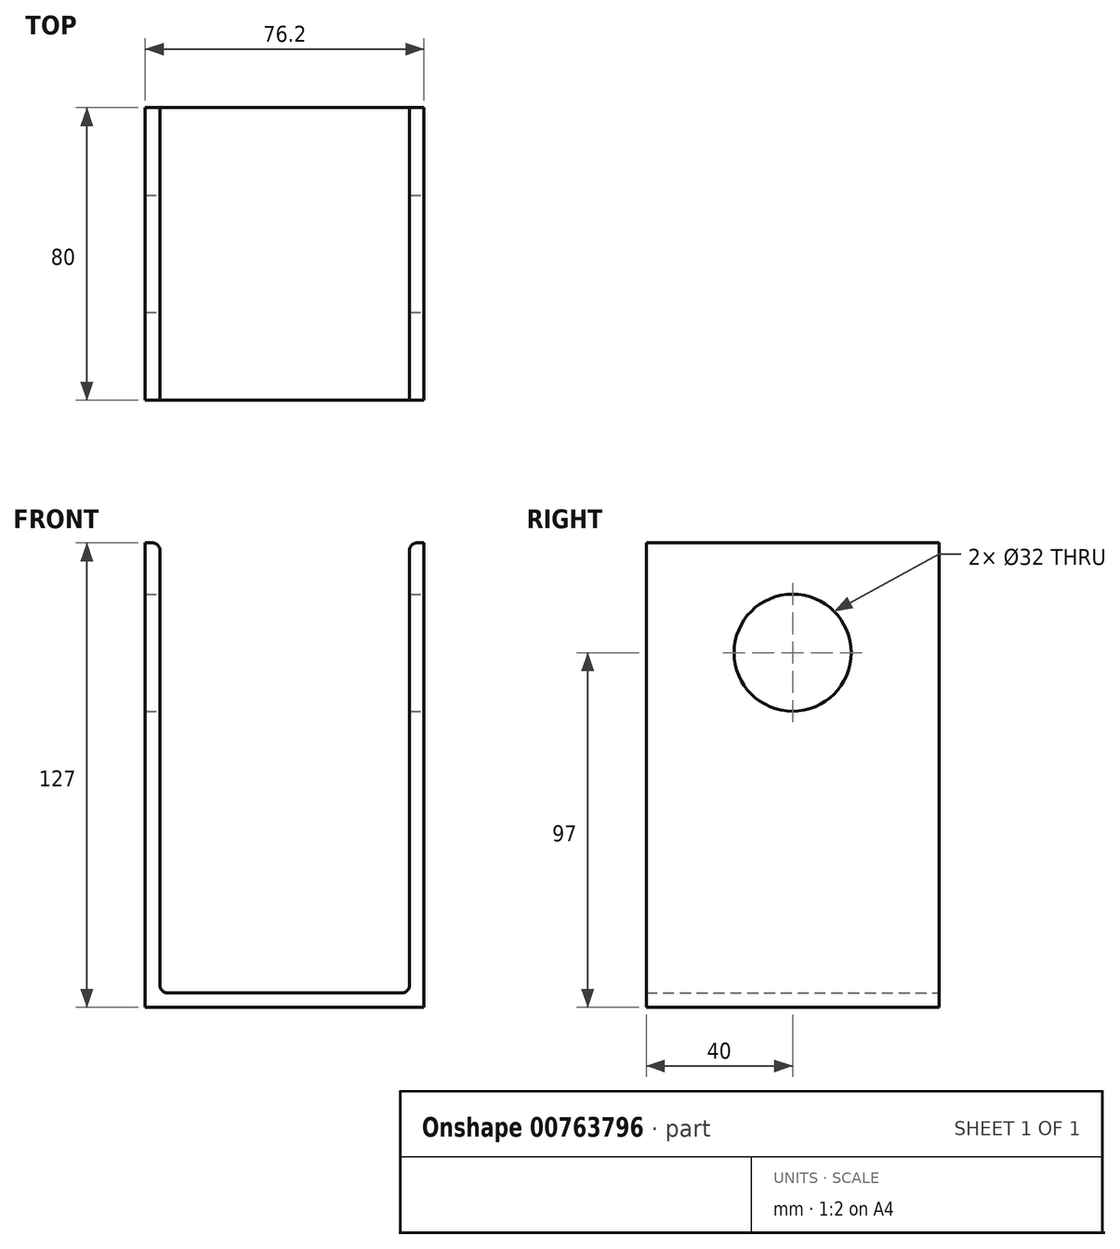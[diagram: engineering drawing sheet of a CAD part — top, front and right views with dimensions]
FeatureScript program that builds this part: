
annotation { "Feature Type Name" : "Feature", "Feature Type Description" : "" }
export const myFeature = defineFeature(function(context is Context, id is Id, definition is map)
    precondition{}
    {
        {
            var Q0;
            Q0=qCreatedBy(makeId("Front.planeOp"),FACE);
            var sketch = newSketch(context, id + "F0", { "sketchPlane" : qUnion([Q0])});
            skLineSegment(sketch, "E0", {"start": v(-38.1, 0) * mm, "end": v(0, 0) * mm});
            skLineSegment(sketch, "E1", {"start": v(-38.1, 0) * mm, "end": v(-38.1, 127) * mm});
            skLineSegment(sketch, "E2.0", {"start": v(-34.1, 6) * mm, "end": v(-34.1, 125) * mm});
            skLineSegment(sketch, "E2.1", {"start": v(-32.1, 4) * mm, "end": v(0, 4) * mm});
            skLineSegment(sketch, "E3", {"start": v(-38.1, 127) * mm, "end": v(-36.1, 127) * mm});
            skPoint(sketch, "E4.visualSharp", {"position": v(-34.1, 127) * mm});
            skArc(sketch, "E4.filletArc", {"start": v(-34.1, 125) * mm, "mid": v(-34.69, 126.41) * mm, "end": v(-36.1, 127) * mm});
            skPoint(sketch, "E5.visualSharp", {"position": v(-34.1, 4) * mm});
            skArc(sketch, "E5.filletArc", {"start": v(-34.1, 6) * mm, "mid": v(-33.51, 4.59) * mm, "end": v(-32.1, 4) * mm});
            skArc(sketch, "E6.MirrorCS", {"start": v(34.1, 6) * mm, "mid": v(33.51, 4.59) * mm, "end": v(32.1, 4) * mm});
            skLineSegment(sketch, "E7.MirrorCS", {"start": v(38.1, 127) * mm, "end": v(36.1, 127) * mm});
            skArc(sketch, "E8.MirrorCS", {"start": v(34.1, 125) * mm, "mid": v(34.69, 126.41) * mm, "end": v(36.1, 127) * mm});
            skLineSegment(sketch, "E9.MirrorCS", {"start": v(38.1, 0) * mm, "end": v(38.1, 127) * mm});
            skLineSegment(sketch, "E10.MirrorCS", {"start": v(34.1, 6) * mm, "end": v(34.1, 125) * mm});
            skPoint(sketch, "E11.MirrorP", {"position": v(34.1, 127) * mm});
            skPoint(sketch, "E12.MirrorP", {"position": v(34.1, 4) * mm});
            skLineSegment(sketch, "E13.MirrorCS", {"start": v(32.1, 4) * mm, "end": v(0, 4) * mm});
            skLineSegment(sketch, "E14.MirrorCS", {"start": v(38.1, 0) * mm, "end": v(0, 0) * mm});
            skSolve(sketch);
        }
        {
            var Q0;
            Q0=makeQuery(id+"F0.imprint","IMPRINT",FACE,{"disambiguationData":[TD([[makeQuery(id+"F0.imprint","IMPRINT",EDGE,{"derivedFrom":sQuery(id+"F0.wireOp",EDGE,"E0")}),1.0]])]});
            extrude(context, id + "F1", {"entities" : qUnion([Q0]), "depth" : 80 * mm, "offsetDistance" : 25 * mm});
        }
        {
            var Q0;
            Q0=makeQuery(id+"F1.opExtrude","SWEPT_FACE",FACE,{"disambiguationData":[OSD([sQuery(id+"F0.wireOp",EDGE,"E9.MirrorCS")])]});
            var sketch = newSketch(context, id + "F2", { "sketchPlane" : qUnion([Q0])});
            skCircle(sketch, "E15", {"center": v(-40, 97) * mm, "radius": 16 * mm});
            skPoint(sketch, "E15.centerSnap0", {"position": v(-40, 127) * mm});
            skSolve(sketch);
        }
        {
            var Q0;
            Q0 = qSketchRegion(id + "F2", true);
            extrude(context, id + "F3", {"entities" : qUnion([Q0]), "operationType" : NewBodyOperationType.REMOVE, "oppositeDirection" : true, "depth" : 85 * mm, "offsetDistance" : 25 * mm});
        }
    });
